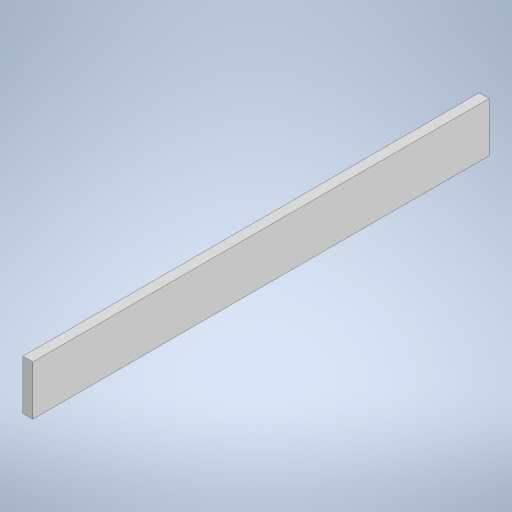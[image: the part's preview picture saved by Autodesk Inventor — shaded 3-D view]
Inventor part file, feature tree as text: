
AUTODESK INVENTOR PART (.ipt)
format: ipt  version: 2024.3 (Build 283343000, 343)  size: 221,696 bytes
history: native  units: mm
features: extrude x1, sketch x1
ambient origin geometry x8: Origin, YZ Plane, XZ Plane, XY Plane, X Axis, Y Axis, Z Axis, Center Point
bodies: Solid1 (feature_tree)
feature tree (2):
  extrude  "Extrusion1"  Depth=92.0mm
  sketch  "Sketch1"  dims[d0=10.0mm d1=92.0mm d2=2.0mm d3=0.0mm d4=0.5mm d5=0.872665mm]
